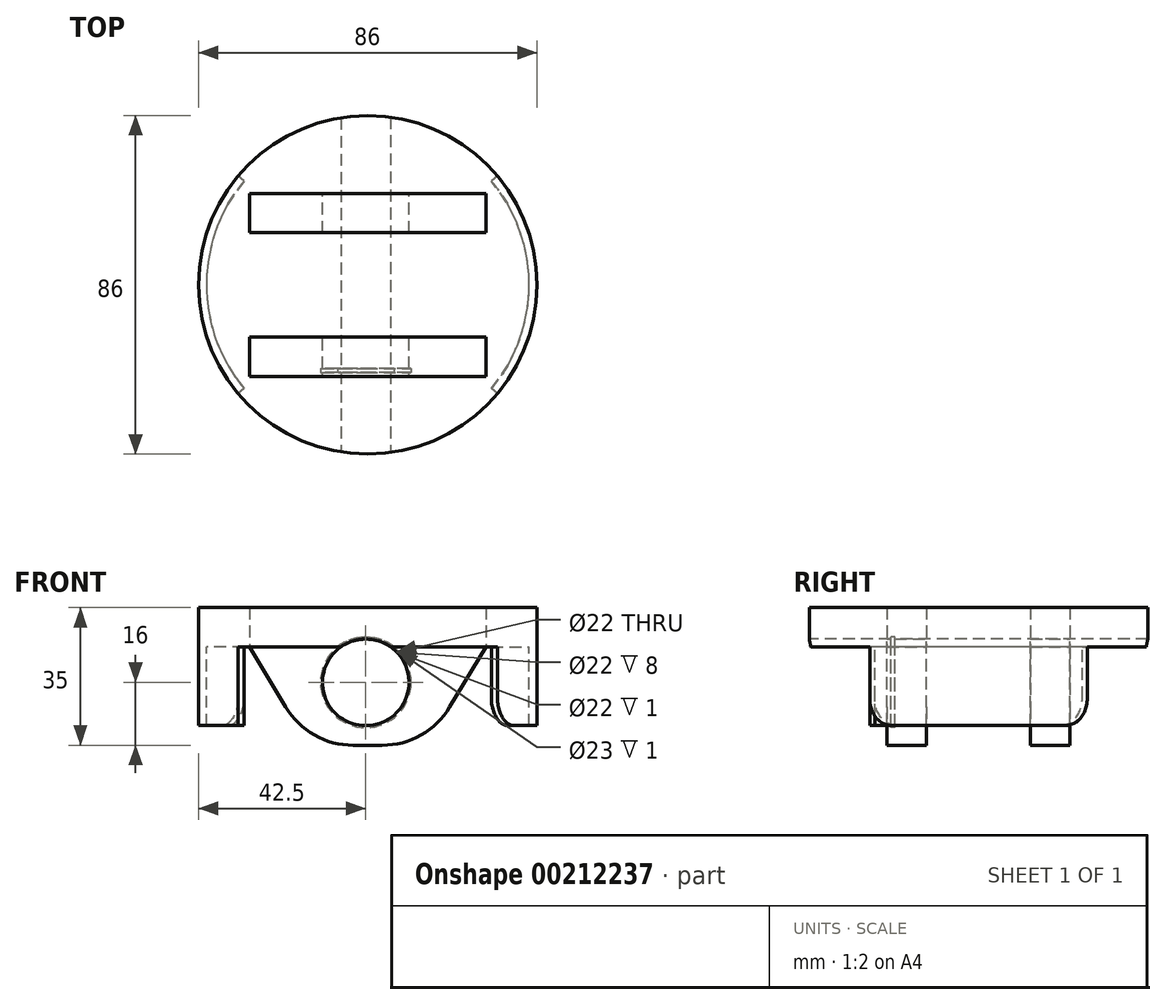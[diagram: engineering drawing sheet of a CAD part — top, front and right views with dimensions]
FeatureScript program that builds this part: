
annotation { "Feature Type Name" : "Feature", "Feature Type Description" : "" }
export const myFeature = defineFeature(function(context is Context, id is Id, definition is map)
    precondition{}
    {
        {
            var Q0;
            Q0=qCreatedBy(makeId("Front.planeOp"),FACE);
            var sketch = newSketch(context, id + "F0", { "sketchPlane" : qUnion([Q0])});
            skLineSegment(sketch, "E0.bottom", {"start": v(-30, 5) * mm, "end": v(30, 5) * mm});
            skLineSegment(sketch, "E0.left", {"start": v(-30, 5) * mm, "end": v(-30, -5) * mm});
            skLineSegment(sketch, "E0.right", {"start": v(30, 5) * mm, "end": v(30, -5) * mm});
            skPoint(sketch, "E0.middle", {"position": v(0, 0) * mm});
            skCircle(sketch, "E1", {"center": v(-0.5, -14) * mm, "radius": 11 * mm});
            skLineSegment(sketch, "E2", {"start": v(-30, -5) * mm, "end": v(-20.83, -20.29) * mm});
            skLineSegment(sketch, "E3", {"start": v(-3.68, -30) * mm, "end": v(3.68, -30) * mm});
            skLineSegment(sketch, "E4", {"start": v(20.83, -20.29) * mm, "end": v(30, -5) * mm});
            skPoint(sketch, "E5.visualSharp", {"position": v(-15, -30) * mm});
            skPoint(sketch, "E6.visualSharp", {"position": v(15, -30) * mm});
            skArc(sketch, "E7.filletArc", {"start": v(-20.83, -20.29) * mm, "mid": v(-13.53, -27.4) * mm, "end": v(-3.68, -30) * mm});
            skArc(sketch, "E8.filletArc", {"start": v(3.68, -30) * mm, "mid": v(13.53, -27.4) * mm, "end": v(20.83, -20.29) * mm});
            skSolve(sketch);
        }
        {
            var Q0;
            Q0=qCreatedBy(makeId("Front.planeOp"),FACE);
            var sketch = newSketch(context, id + "F1", { "sketchPlane" : qUnion([Q0])});
            skLineSegment(sketch, "E9", {"start": v(0, 5) * mm, "end": v(-43, 5) * mm});
            skLineSegment(sketch, "E10", {"start": v(-43, 5) * mm, "end": v(-43, -5) * mm});
            skLineSegment(sketch, "E11", {"start": v(-43, -5) * mm, "end": v(0, -5) * mm});
            skLineSegment(sketch, "E12", {"start": v(0, 5) * mm, "end": v(0, -5) * mm});
            skSolve(sketch);
        }
        {
            var Q0;
            Q0=makeQuery(id+"F0.imprint","IMPRINT",FACE,{"disambiguationData":[TD([[makeQuery(id+"F0.imprint","IMPRINT",EDGE,{"derivedFrom":sQuery(id+"F0.wireOp",EDGE,"E0.bottom")}),-1.0]])]});
            extrude(context, id + "F2", {"entities" : qUnion([Q0]), "endBound" : BoundingType.SYMMETRIC, "depth" : (26.5 + 20) * mm});
        }
        {
            var Q0;
            Q0 = qSketchRegion(id + "F0", true);
            extrude(context, id + "F3", {"entities" : qUnion([Q0]), "operationType" : NewBodyOperationType.REMOVE, "endBound" : BoundingType.SYMMETRIC, "oppositeDirection" : true, "depth" : 26.5 * mm});
        }
        {
            var Q0;
            Q0 = qSketchRegion(id + "F1", true);
            var Q1;
            Q1=sQuery(id+"F1.wireOp",EDGE,"E12");
            revolve(context, id + "F4", {"entities" : qUnion([Q0]), "axis" : qUnion([Q1]), "revolveType" : RevolveType.FULL});
        }
        {
            var Q0;
            Q0=makeQuery(id+"F0.imprint","IMPRINT",FACE,{"disambiguationData":[TD([[makeQuery(id+"F0.imprint","IMPRINT",EDGE,{"derivedFrom":sQuery(id+"F0.wireOp",EDGE,"E1")}),1.0]])]});
            extrude(context, id + "F5", {"entities" : qUnion([Q0]), "operationType" : NewBodyOperationType.REMOVE, "endBound" : BoundingType.SYMMETRIC, "oppositeDirection" : true, "depth" : 86 * mm});
        }
        {
            var Q0;
            Q0=qCreatedBy(makeId("Front.planeOp"),FACE);
            var sketch = newSketch(context, id + "F6", { "sketchPlane" : qUnion([Q0])});
            skLineSegment(sketch, "E13", {"start": v(-43, 5) * mm, "end": v(-43, -25) * mm});
            skLineSegment(sketch, "E14", {"start": v(-43, -25) * mm, "end": v(-41, -25) * mm});
            skLineSegment(sketch, "E15", {"start": v(-41, -25) * mm, "end": v(-41, -5) * mm});
            skLineSegment(sketch, "E16", {"start": v(0, 25.88) * mm, "end": v(0, -41.46) * mm, "construction": true});
            skLineSegment(sketch, "E17", {"start": v(-43, 5) * mm, "end": v(-41, -5) * mm});
            skLineSegment(sketch, "E18.MirrorCS", {"start": v(43, 5) * mm, "end": v(41, -5) * mm});
            skLineSegment(sketch, "E19.MirrorCS", {"start": v(41, -25) * mm, "end": v(41, -5) * mm});
            skLineSegment(sketch, "E20.MirrorCS", {"start": v(43, -25) * mm, "end": v(41, -25) * mm});
            skLineSegment(sketch, "E21.MirrorCS", {"start": v(43, 5) * mm, "end": v(43, -25) * mm});
            skSolve(sketch);
        }
        {
            var Q0;
            Q0 = qSketchRegion(id + "F6", true);
            var Q1;
            Q1=sQuery(id+"F6.wireOp",EDGE,"E16");
            revolve(context, id + "F7", {"operationType" : NewBodyOperationType.ADD, "entities" : qUnion([Q0]), "axis" : qUnion([Q1]), "revolveType" : RevolveType.SYMMETRIC, "angle" : 80 * degree});
        }
        {
            var Q0;
            Q0=makeQuery(id+"F2.opExtrude","CAP_FACE",FACE,{"disambiguationData":[OSD([sQuery(id+"F0.wireOp",EDGE,"E0.bottom"),sQuery(id+"F0.wireOp",EDGE,"E0.left"),sQuery(id+"F0.wireOp",EDGE,"E0.right"),sQuery(id+"F0.wireOp",EDGE,"E1"),sQuery(id+"F0.wireOp",EDGE,"E2"),sQuery(id+"F0.wireOp",EDGE,"E3"),sQuery(id+"F0.wireOp",EDGE,"E4"),sQuery(id+"F0.wireOp",EDGE,"E5.filletArc"),sQuery(id+"F0.wireOp",EDGE,"E6.filletArc")])],"isStart":false});
            cPlane(context, id + "F8", {"entities" : qUnion([Q0]), "cplaneType" : CPlaneType.OFFSET, "offset" : 1 * mm, "oppositeDirection" : true, "width" : 150 * mm, "height" : 150 * mm});
        }
        {
            var Q0;
            Q0=qCreatedBy(id+"F8.planeOp",FACE);
            var sketch = newSketch(context, id + "F9", { "sketchPlane" : qUnion([Q0])});
            skCircle(sketch, "E22", {"center": v(-0.5, -14) * mm, "radius": 11.5 * mm});
            skCircle(sketch, "E23", {"center": v(-0.5, -14) * mm, "radius": 11 * mm});
            skSolve(sketch);
        }
        {
            var Q0;
            Q0 = qSketchRegion(id + "F9", true);
            extrude(context, id + "F10", {"entities" : qUnion([Q0]), "operationType" : NewBodyOperationType.REMOVE, "oppositeDirection" : true, "depth" : 1 * mm});
        }
        {
            var Q0;
            Q0=makeQuery(id+"F7.opRevolve","CAP_EDGE",EDGE,{"disambiguationData":[OSD([sQuery(id+"F6.wireOp",EDGE,"E14")]),OD(1.0)],"isStart":false});
            var Q1;
            Q1=makeQuery(id+"F7.opRevolve","CAP_EDGE",EDGE,{"disambiguationData":[OSD([sQuery(id+"F6.wireOp",EDGE,"E20.MirrorCS")])],"isStart":true});
            var Q2;
            Q2=makeQuery(id+"F7.opRevolve","CAP_EDGE",EDGE,{"disambiguationData":[OSD([sQuery(id+"F6.wireOp",EDGE,"E20.MirrorCS")])],"isStart":false});
            var Q3;
            Q3=makeQuery(id+"F7.opRevolve","CAP_EDGE",EDGE,{"disambiguationData":[OSD([sQuery(id+"F6.wireOp",EDGE,"E14")]),OD(0.0)],"isStart":false});
            fillet(context, id + "F11", {"entities" : qUnion([Q0, Q1, Q2, Q3]), "radius" : 7 * mm, "tangentPropagation" : true, "allowEdgeOverflow" : false});
        }
    });
